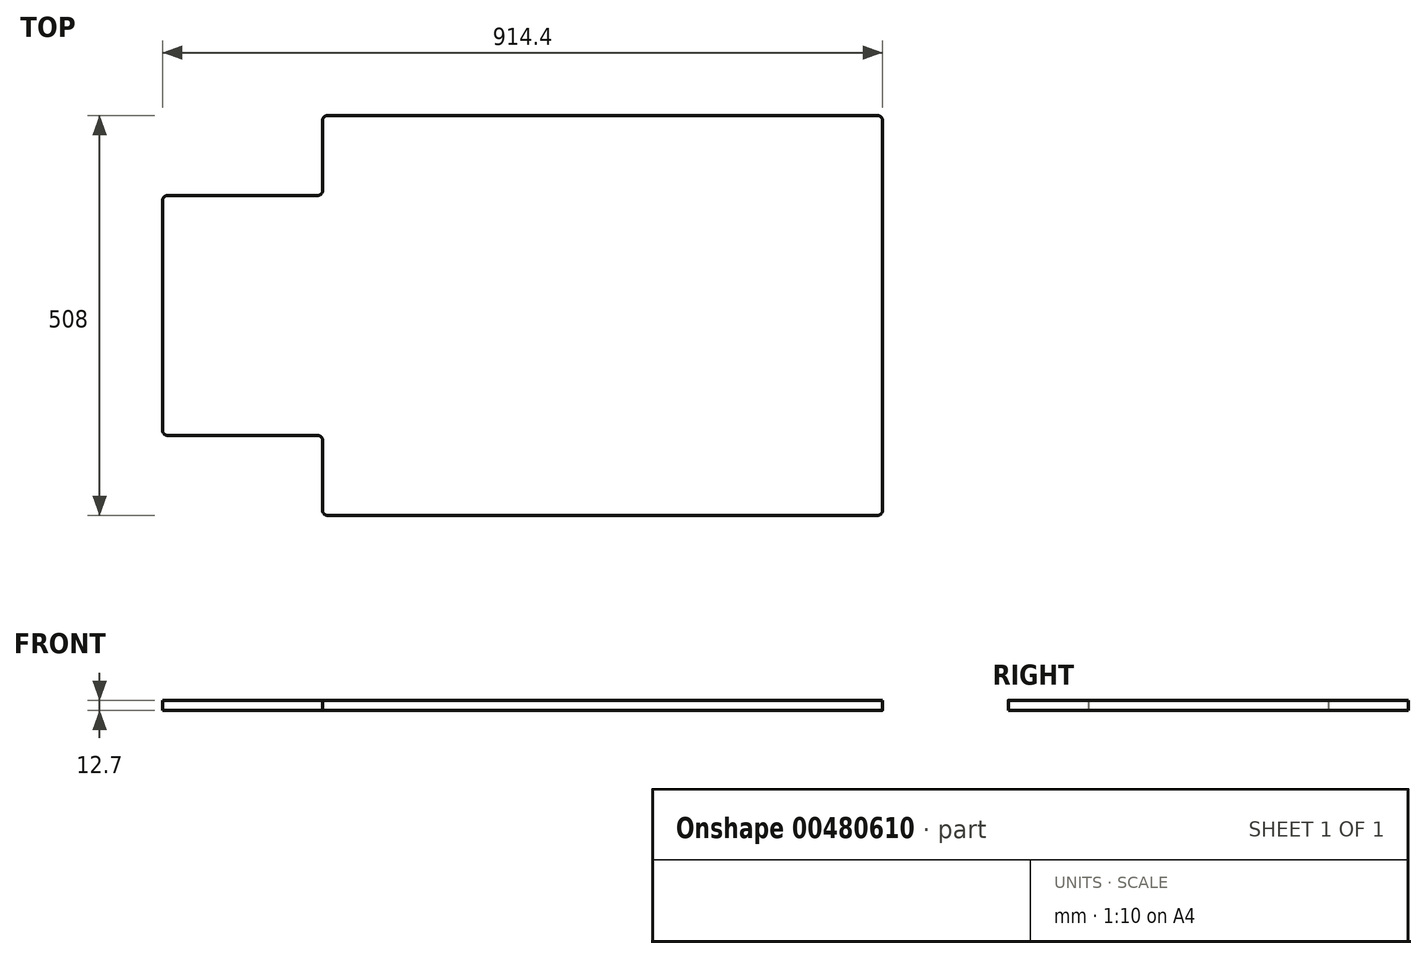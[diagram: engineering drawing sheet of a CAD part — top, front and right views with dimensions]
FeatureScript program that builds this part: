
annotation { "Feature Type Name" : "Feature", "Feature Type Description" : "" }
export const myFeature = defineFeature(function(context is Context, id is Id, definition is map)
    precondition{}
    {
        {
            var Q0;
            Q0=qCreatedBy(makeId("Top.planeOp"),FACE);
            var sketch = newSketch(context, id + "F0", { "sketchPlane" : qUnion([Q0])});
            skLineSegment(sketch, "E0.bottom", {"start": v(-254, -254) * mm, "end": v(457.2, -254) * mm});
            skLineSegment(sketch, "E0.top", {"start": v(-254, 254) * mm, "end": v(457.2, 254) * mm});
            skLineSegment(sketch, "E0.left", {"start": v(-457.2, -152.4) * mm, "end": v(-457.2, 152.4) * mm});
            skLineSegment(sketch, "E0.right", {"start": v(457.2, -254) * mm, "end": v(457.2, 254) * mm});
            skPoint(sketch, "E0.middle", {"position": v(0, 0) * mm});
            skLineSegment(sketch, "E1", {"start": v(-457.2, 152.4) * mm, "end": v(-254, 152.4) * mm});
            skLineSegment(sketch, "E2", {"start": v(-254, 152.4) * mm, "end": v(-254, 254) * mm});
            skLineSegment(sketch, "E3", {"start": v(-457.2, -152.4) * mm, "end": v(-254, -152.4) * mm});
            skLineSegment(sketch, "E4", {"start": v(-254, -152.4) * mm, "end": v(-254, -254) * mm});
            skPoint(sketch, "E5.orphan", {"position": v(-457.2, -254) * mm});
            skPoint(sketch, "E6.orphan", {"position": v(-457.2, 254) * mm});
            skSolve(sketch);
        }
        {
            var Q0;
            Q0 = qSketchRegion(id + "F0", true);
            extrude(context, id + "F1", {"entities" : qUnion([Q0]), "depth" : 12.7 * mm});
        }
        {
            var Q0;
            Q0=makeQuery(id+"F1.opExtrude","SWEPT_EDGE",EDGE,{"disambiguationData":[OSD([sQuery(id+"F0.wireOp",EDGE,"E3"),sQuery(id+"F0.wireOp",EDGE,"E4")])]});
            var Q1;
            Q1=makeQuery(id+"F1.opExtrude","SWEPT_EDGE",EDGE,{"disambiguationData":[OSD([sQuery(id+"F0.wireOp",EDGE,"E0.left"),sQuery(id+"F0.wireOp",EDGE,"E3")])]});
            var Q2;
            Q2=makeQuery(id+"F1.opExtrude","SWEPT_EDGE",EDGE,{"disambiguationData":[OSD([sQuery(id+"F0.wireOp",EDGE,"E0.left"),sQuery(id+"F0.wireOp",EDGE,"E1")])]});
            var Q3;
            Q3=makeQuery(id+"F1.opExtrude","SWEPT_EDGE",EDGE,{"disambiguationData":[OSD([sQuery(id+"F0.wireOp",EDGE,"E1"),sQuery(id+"F0.wireOp",EDGE,"E2")])]});
            var Q4;
            Q4=makeQuery(id+"F1.opExtrude","SWEPT_EDGE",EDGE,{"disambiguationData":[OSD([sQuery(id+"F0.wireOp",EDGE,"E0.top"),sQuery(id+"F0.wireOp",EDGE,"E2")])]});
            var Q5;
            Q5=makeQuery(id+"F1.opExtrude","SWEPT_EDGE",EDGE,{"disambiguationData":[OSD([sQuery(id+"F0.wireOp",EDGE,"E0.bottom"),sQuery(id+"F0.wireOp",EDGE,"E4")])]});
            var Q6;
            Q6=makeQuery(id+"F1.opExtrude","SWEPT_EDGE",EDGE,{"disambiguationData":[OSD([sQuery(id+"F0.wireOp",EDGE,"E0.bottom"),sQuery(id+"F0.wireOp",EDGE,"E0.right")])]});
            var Q7;
            Q7=makeQuery(id+"F1.opExtrude","SWEPT_EDGE",EDGE,{"disambiguationData":[OSD([sQuery(id+"F0.wireOp",EDGE,"E0.top"),sQuery(id+"F0.wireOp",EDGE,"E0.right")])]});
            fillet(context, id + "F2", {"entities" : qUnion([Q0, Q1, Q2, Q3, Q4, Q5, Q6, Q7]), "radius" : 6.35 * mm, "tangentPropagation" : true, "allowEdgeOverflow" : false});
        }
    });
